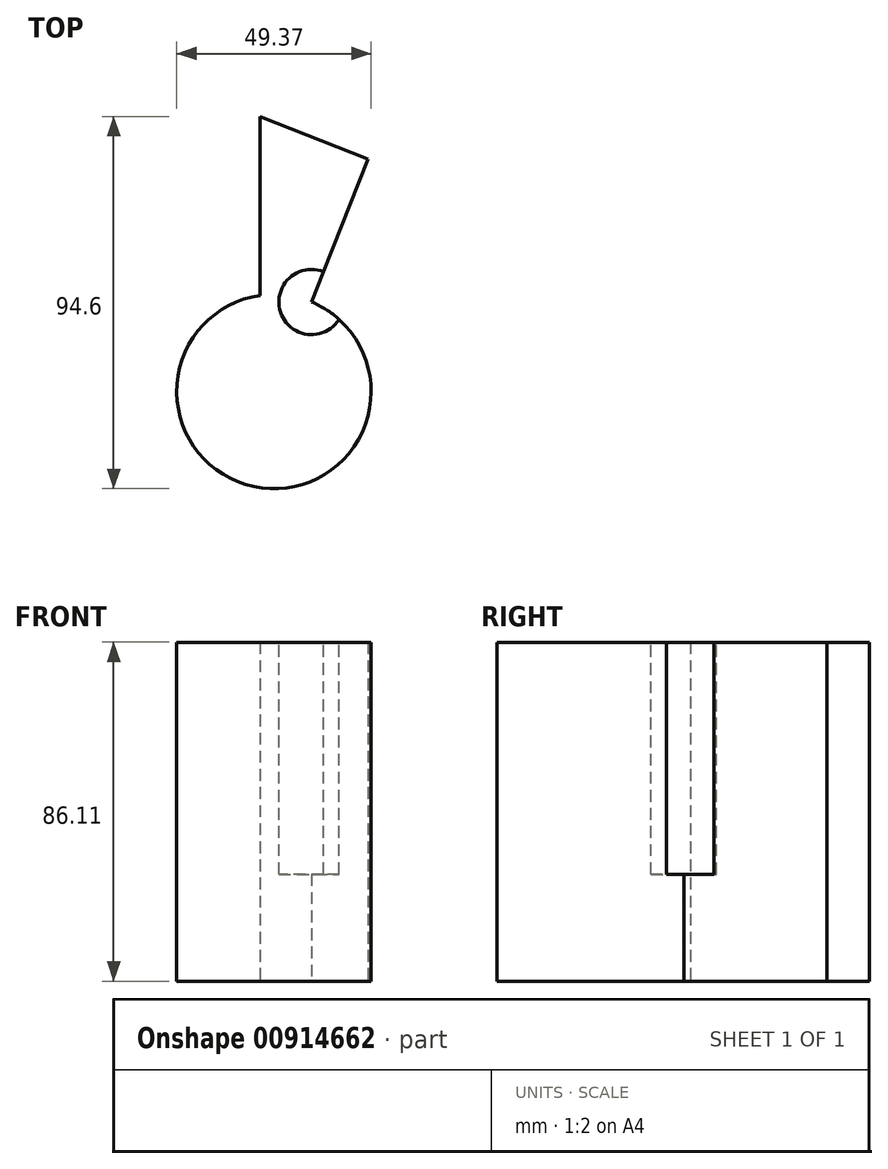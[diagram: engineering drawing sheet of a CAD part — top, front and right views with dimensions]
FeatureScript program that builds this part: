
annotation { "Feature Type Name" : "Feature", "Feature Type Description" : "" }
export const myFeature = defineFeature(function(context is Context, id is Id, definition is map)
    precondition{}
    {
        {
            var Q0;
            Q0=qCreatedBy(makeId("Top.planeOp"),FACE);
            var sketch = newSketch(context, id + "F0", { "sketchPlane" : qUnion([Q0])});
            skArc(sketch, "E0", {"start": v(-119.39, 36.1) * mm, "mid": v(-119.02, -12.82) * mm, "end": v(-106.33, 34.43) * mm});
            skLineSegment(sketch, "E1", {"start": v(-106.33, 34.43) * mm, "end": v(-92, 70.76) * mm});
            skLineSegment(sketch, "E2", {"start": v(-92, 70.76) * mm, "end": v(-119.39, 81.58) * mm});
            skLineSegment(sketch, "E3", {"start": v(-119.39, 81.58) * mm, "end": v(-119.39, 36.1) * mm});
            skSolve(sketch);
        }
        {
            var Q0;
            Q0=makeQuery(id+"F0.imprint","IMPRINT",FACE,{"disambiguationData":[TD([[makeQuery(id+"F0.imprint","IMPRINT",EDGE,{"derivedFrom":sQuery(id+"F0.wireOp",EDGE,"E0")}),1.0]])]});
            extrude(context, id + "F1", {"entities" : qUnion([Q0]), "depth" : 86.1 * mm, "offsetDistance" : 25.4 * mm});
        }
        {
            var Q0;
            Q0=makeQuery(id+"F1.opExtrude","CAP_FACE",FACE,{"disambiguationData":[OSD([sQuery(id+"F0.wireOp",EDGE,"E0"),sQuery(id+"F0.wireOp",EDGE,"E1"),sQuery(id+"F0.wireOp",EDGE,"E2"),sQuery(id+"F0.wireOp",EDGE,"E3")])],"isStart":false});
            var sketch = newSketch(context, id + "F2", { "sketchPlane" : qUnion([Q0])});
            skCircle(sketch, "E4", {"center": v(-106.33, 34.43) * mm, "radius": 8.29 * mm});
            skSolve(sketch);
        }
        {
            var Q0;
            {var subQ0=sQuery(id+"F2.wireOp",EDGE,"E4");var subQ1=makeQuery(id+"F1.opExtrude","CAP_EDGE",EDGE,{"disambiguationData":[OSD([sQuery(id+"F0.wireOp",EDGE,"E0")])],"isStart":false});var subQ2=makeQuery(id+"F2.imprint","INTERSECT",VERTEX,{"derivedFrom":[subQ1,subQ0]});Q0=makeQuery(id+"F2.imprint","IMPRINT",FACE,{"disambiguationData":[TD([[makeQuery(id+"F2.imprint","IMPRINT",EDGE,{"disambiguationData":[TD([[subQ2,1.0]])],"derivedFrom":subQ0}),1.0]])]});}
            extrude(context, id + "F3", {"entities" : qUnion([Q0]), "operationType" : NewBodyOperationType.REMOVE, "oppositeDirection" : true, "depth" : 58.93 * mm, "offsetDistance" : 25.4 * mm});
        }
    });
